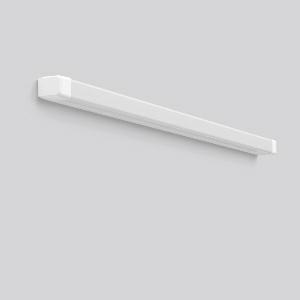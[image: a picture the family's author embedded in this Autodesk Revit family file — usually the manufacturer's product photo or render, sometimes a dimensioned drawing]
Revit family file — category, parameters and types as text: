
# Revit family: baleva_451203_002_2_592f
name_source: partatom
category: Lighting Fixtures
units: mm (PartAtom-declared; Revit-internal decimal feet)

## family parameters
Cut with Voids When Loaded = No
Host = Face
Light Source = No
Part Type = Normal
Room Calculation Point = No
Round Connector Dimension = Use Diameter
Shared = No

## types (1)
- MultiColor 830 (1 x LED Modul 830, 2100 lm, 3000)
    Apparent Load = 19 VA
    CIE Flux Codes = 40 69 88 82 100
    Color Rendering = 80
    Color Temperature = 3000
    Default Elevation = 1800 mm
    Description = Series: BALEVA
Linear luminaire with timeless functional design. Ideal for sanitary areas, corridors, waiting areas, nursing homes, patient rooms. Body and end caps made of white plastic. Diffuser made of plastic (polycarbonate), opal, shockproof. Homogeneous and smooth light distribution. MultiColour: With rear switching element, variable colour temperature 3000  K or 4000  K. Factory setting is 4000 K. Diffuser can be assembled without the use of tools. Quick and easy to install. Can be installed horizontally and vertically. 2 central cable inlets for looping the cable. Converter integrated and encapsulated. 
Colour: white
Length: 1200 mm
Width: 46 mm
Height: 60 mm
Lamp: LED
Socket: without socket
Colour temperature: 3000K, 4000K
Colour rendering index (CRI): 80
System power: 19 W
Rated luminous flux: 2100 lm
Luminous efficiency: 111 lm/W
System power 2: 19 W
Rated luminous flux 2: 2200 lm
Luminous efficiency 2: 116 lm/W
Control gear: Regulated power supply
Protection class: II
Type of protection: IP 40
    Height = 60 mm  [stored 0.19685 ft]
    Lamp = 1 x LED Modul 830
    Lamp Light Flux = 2100 lm
    Lamp count = 1
    Length = 1200 mm
    Lifetime = 50000 h
    Luminous efficacy = 111 lm/W
    Manufacturer = RZB
    ModVariant = No
    Model = 451203.002.2
    Mounting Place = Ceiling, Wall
    Mounting Type = Surface mounted
    Number of Poles = 1
    OnlyDefault = Yes
    Power Factor = 1
    Product Name = BALEVA
    Product group = Surface mounted ceiling and wall luminaires
    ProductGroupID = 305
    Protection Class = Protection class II
    Protection Degree = IP 40
    RLX_Detail_Level = 1
    RLX_Emergency_Light_Flux = 0 lm
    RLX_Emergency_Type = 0
    RLX_Emergency_Type_DB = No
    RlxData = <blob elided: 42641 chars, md5=182eb321>
    Socket = socket
    Standby Power = 0 W
    System Light Flux = 2100 lm
    System Power = 19 W
    Type Comments = MultiColor 830
    Type Image = 451203.002.jpg
    URL = http://relux.com
    VarID = multicolor_830
    Voltage = 230 V
    Voltage Range = 220-240 V
    Weight = 0.00 kg
    Width = 46 mm

note: [stored X ft] marks values corroborated as IEEE doubles in the binary element streams (Revit-internal decimal feet)

## geometry (parser evidence)
native form markers: Blend x4, Sweep x10
no freeform markers — native parametric forms only
